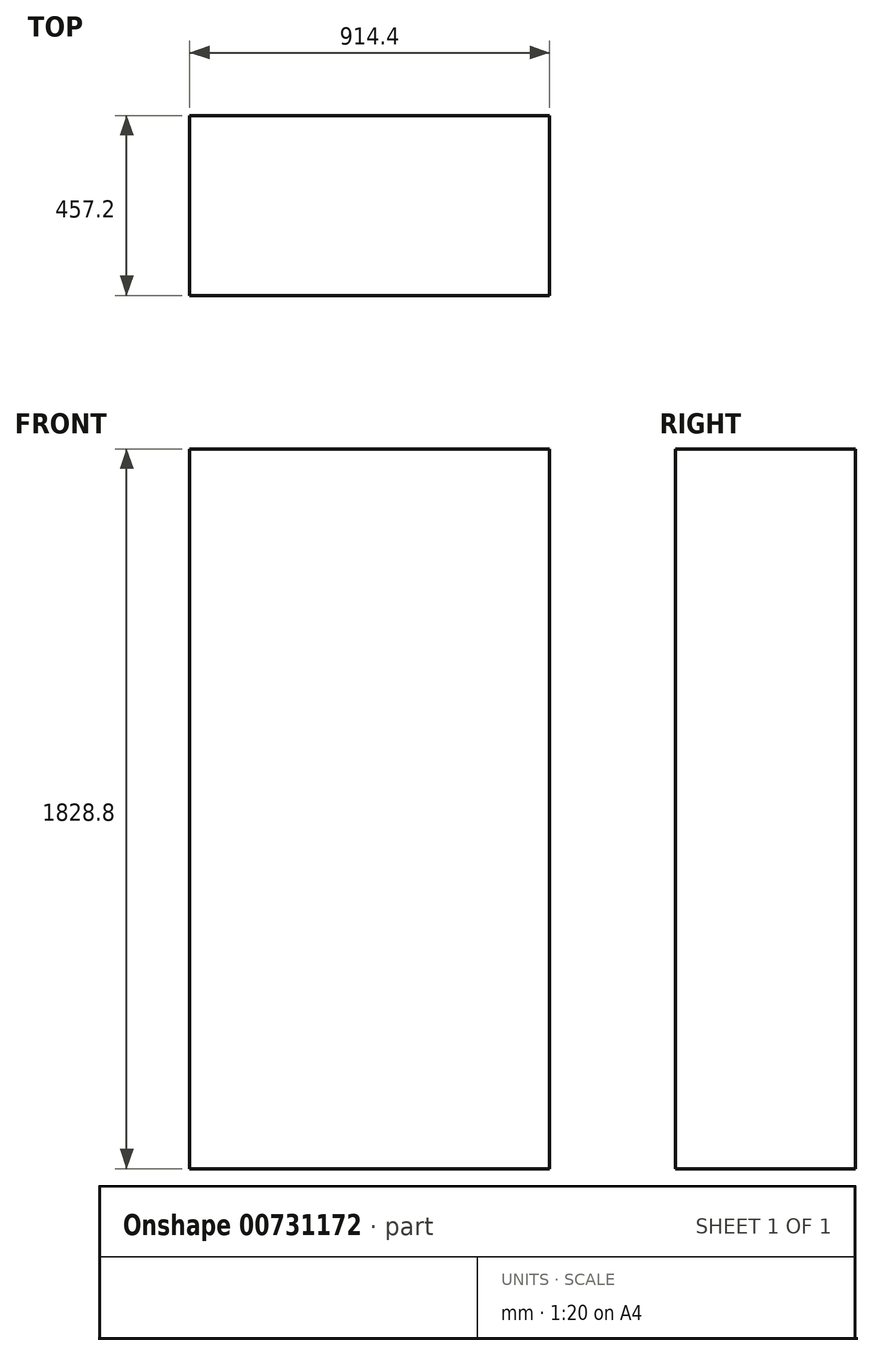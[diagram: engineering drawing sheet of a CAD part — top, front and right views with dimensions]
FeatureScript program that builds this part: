
annotation { "Feature Type Name" : "Feature", "Feature Type Description" : "" }
export const myFeature = defineFeature(function(context is Context, id is Id, definition is map)
    precondition{}
    {
        {
            var Q0;
            Q0=qCreatedBy(makeId("Front.planeOp"),FACE);
            var sketch = newSketch(context, id + "F0", { "sketchPlane" : qUnion([Q0])});
            skLineSegment(sketch, "E0.bottom", {"start": v(-457.2, 914.4) * mm, "end": v(457.2, 914.4) * mm});
            skLineSegment(sketch, "E0.top", {"start": v(-457.2, -914.4) * mm, "end": v(457.2, -914.4) * mm});
            skLineSegment(sketch, "E0.left", {"start": v(-457.2, 914.4) * mm, "end": v(-457.2, -914.4) * mm});
            skLineSegment(sketch, "E0.right", {"start": v(457.2, 914.4) * mm, "end": v(457.2, -914.4) * mm});
            skPoint(sketch, "E0.middle", {"position": v(0, 0) * mm});
            skSolve(sketch);
        }
        {
            var Q0;
            Q0 = qSketchRegion(id + "F0", true);
            extrude(context, id + "F1", {"entities" : qUnion([Q0]), "depth" : 457.2 * mm, "offsetDistance" : 25.4 * mm});
        }
    });
